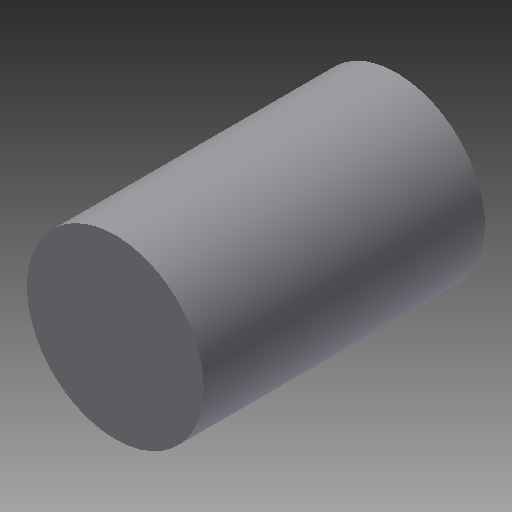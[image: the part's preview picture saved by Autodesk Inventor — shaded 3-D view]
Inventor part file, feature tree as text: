
AUTODESK INVENTOR PART (.ipt)
format: ipt  version: 2017 (Build 210142000, 142)  size: 97,792 bytes
history: native  units: in
note: dims shown in document units (in); Inventor stores cm internally (conversion verified against a paired STEP export)
features: plane x1, extrude x1, sketch x1, reference x1
ambient origin geometry x8: Origin, YZ Plane, XZ Plane, XY Plane, X Axis, Y Axis, Z Axis, Center Point
bodies: Solid1 (feature_tree)
feature tree (4):
  plane  "Work Plane1"
  extrude  "Extrusion1"  Depth=3.358in TaperAngle=0.0deg
  sketch  "Sketch1"  dims[d0=2.11in d1=3.358in d2=0.0in]
  reference  "Reference1"
